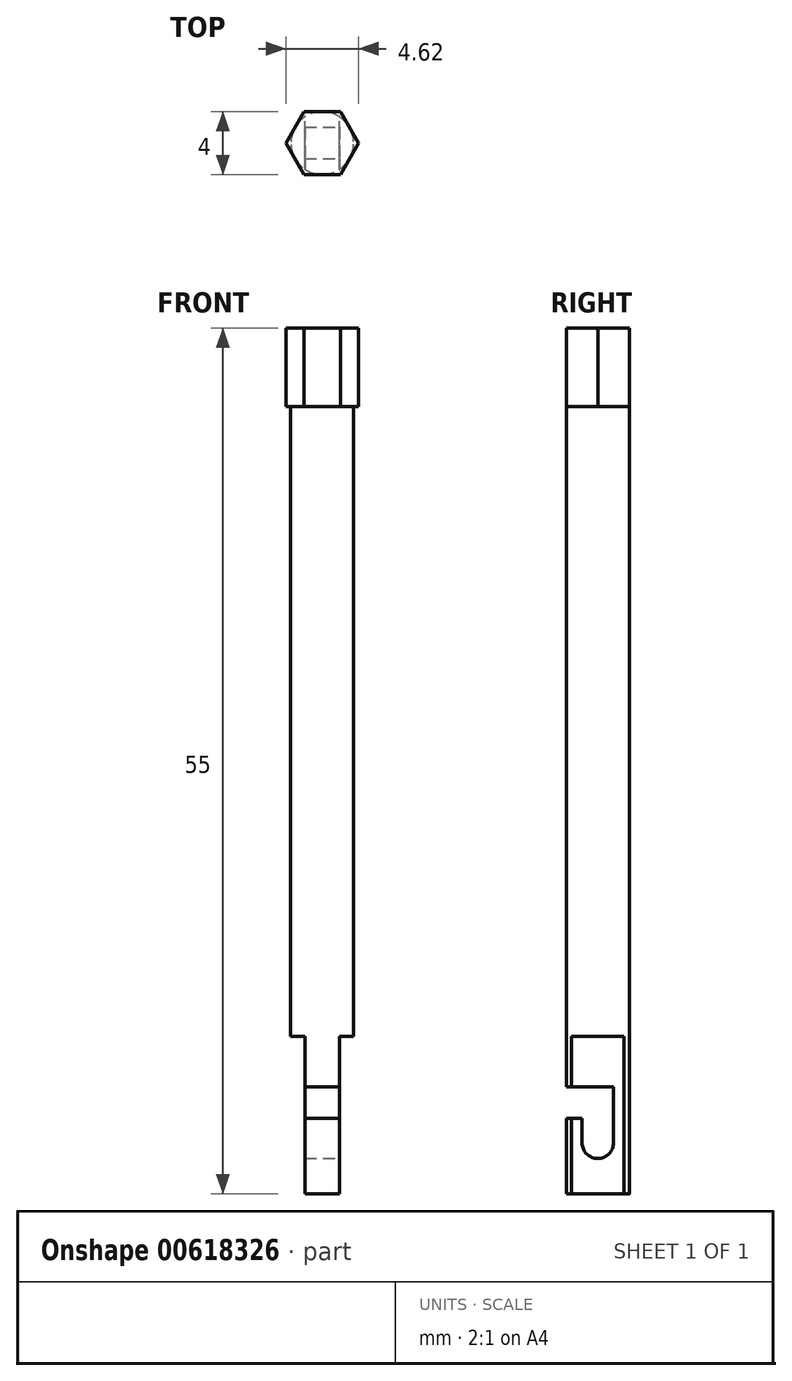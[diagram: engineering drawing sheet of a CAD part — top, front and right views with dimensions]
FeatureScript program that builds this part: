
annotation { "Feature Type Name" : "Feature", "Feature Type Description" : "" }
export const myFeature = defineFeature(function(context is Context, id is Id, definition is map)
    precondition{}
    {
        {
            var Q0;
            Q0=qCreatedBy(makeId("Top.planeOp"),FACE);
            var sketch = newSketch(context, id + "F0", { "sketchPlane" : qUnion([Q0])});
            skCircle(sketch, "E0", {"center": v(0, 0) * mm, "radius": 2 * mm});
            skSolve(sketch);
        }
        {
            var Q0;
            Q0 = qSketchRegion(id + "F0", true);
            extrude(context, id + "F1", {"entities" : qUnion([Q0]), "depth" : 40 * mm, "offsetDistance" : 25 * mm});
        }
        {
            var Q0;
            Q0=makeQuery(id+"F1.opExtrude","CAP_FACE",FACE,{"disambiguationData":[OSD([sQuery(id+"F0.wireOp",EDGE,"E0")])],"isStart":false});
            var sketch = newSketch(context, id + "F2", { "sketchPlane" : qUnion([Q0])});
            skCircle(sketch, "E1.cCircle", {"center": v(0, 0) * mm, "radius": 2 * mm, "construction": true});
            skLineSegment(sketch, "E1.0", {"start": v(-1.15, 2) * mm, "end": v(1.15, 2) * mm});
            skLineSegment(sketch, "E1.1", {"start": v(1.15, 2) * mm, "end": v(2.3, 0) * mm});
            skLineSegment(sketch, "E1.2", {"start": v(2.3, 0) * mm, "end": v(1.15, -2) * mm});
            skLineSegment(sketch, "E1.3", {"start": v(1.15, -2) * mm, "end": v(-1.15, -2) * mm});
            skLineSegment(sketch, "E1.4", {"start": v(-1.15, -2) * mm, "end": v(-2.3, 0) * mm});
            skLineSegment(sketch, "E1.5", {"start": v(-2.3, 0) * mm, "end": v(-1.15, 2) * mm});
            skPoint(sketch, "E1.0.midPoint", {"position": v(0, 2) * mm});
            skSolve(sketch);
        }
        {
            var Q0;
            {var subQ0=sQuery(id+"F2.wireOp",EDGE,"E1.5");var subQ1=sQuery(id+"F2.wireOp",EDGE,"E1.0");var subQ2=makeQuery(id+"F2.imprint","INTERSECT",VERTEX,{"derivedFrom":[subQ1,subQ0]});Q0=makeQuery(id+"F2.imprint","IMPRINT",FACE,{"disambiguationData":[TD([[makeQuery(id+"F2.imprint","IMPRINT",EDGE,{"disambiguationData":[TD([[subQ2,-1.0]])],"derivedFrom":subQ1}),-1.0]])]});}
            var Q1;
            {var subQ0=sQuery(id+"F2.wireOp",EDGE,"E1.5");var subQ1=sQuery(id+"F2.wireOp",EDGE,"E1.4");var subQ2=makeQuery(id+"F2.imprint","INTERSECT",VERTEX,{"derivedFrom":[subQ1,subQ0]});Q1=makeQuery(id+"F2.imprint","IMPRINT",FACE,{"disambiguationData":[TD([[makeQuery(id+"F2.imprint","IMPRINT",EDGE,{"disambiguationData":[TD([[subQ2,1.0]])],"derivedFrom":subQ1}),-1.0]])]});}
            var Q2;
            {var subQ0=sQuery(id+"F2.wireOp",EDGE,"E1.4");var subQ1=sQuery(id+"F2.wireOp",EDGE,"E1.3");var subQ2=makeQuery(id+"F2.imprint","INTERSECT",VERTEX,{"derivedFrom":[subQ1,subQ0]});Q2=makeQuery(id+"F2.imprint","IMPRINT",FACE,{"disambiguationData":[TD([[makeQuery(id+"F2.imprint","IMPRINT",EDGE,{"disambiguationData":[TD([[subQ2,1.0]])],"derivedFrom":subQ1}),-1.0]])]});}
            var Q3;
            {var subQ0=sQuery(id+"F2.wireOp",EDGE,"E1.3");var subQ1=sQuery(id+"F2.wireOp",EDGE,"E1.2");var subQ2=makeQuery(id+"F2.imprint","INTERSECT",VERTEX,{"derivedFrom":[subQ1,subQ0]});Q3=makeQuery(id+"F2.imprint","IMPRINT",FACE,{"disambiguationData":[TD([[makeQuery(id+"F2.imprint","IMPRINT",EDGE,{"disambiguationData":[TD([[subQ2,1.0]])],"derivedFrom":subQ1}),-1.0]])]});}
            var Q4;
            {var subQ0=sQuery(id+"F2.wireOp",EDGE,"E1.2");var subQ1=sQuery(id+"F2.wireOp",EDGE,"E1.1");var subQ2=makeQuery(id+"F2.imprint","INTERSECT",VERTEX,{"derivedFrom":[subQ1,subQ0]});Q4=makeQuery(id+"F2.imprint","IMPRINT",FACE,{"disambiguationData":[TD([[makeQuery(id+"F2.imprint","IMPRINT",EDGE,{"disambiguationData":[TD([[subQ2,1.0]])],"derivedFrom":subQ1}),-1.0]])]});}
            var Q5;
            {var subQ0=sQuery(id+"F2.wireOp",EDGE,"E1.1");var subQ1=sQuery(id+"F2.wireOp",EDGE,"E1.0");var subQ2=makeQuery(id+"F2.imprint","INTERSECT",VERTEX,{"derivedFrom":[subQ1,subQ0]});Q5=makeQuery(id+"F2.imprint","IMPRINT",FACE,{"disambiguationData":[TD([[makeQuery(id+"F2.imprint","IMPRINT",EDGE,{"disambiguationData":[TD([[subQ2,1.0]])],"derivedFrom":subQ1}),-1.0]])]});}
            var Q6;
            {var subQ0=makeQuery(id+"F1.opExtrude","CAP_EDGE",EDGE,{"disambiguationData":[OSD([sQuery(id+"F0.wireOp",EDGE,"E0")])],"isStart":false});var subQ4=makeQuery(id+"F2.imprint","INTERSECT",VERTEX,{"derivedFrom":[subQ0,sQuery(id+"F2.wireOp",EDGE,"E1.0")]});Q6=makeQuery(id+"F2.imprint","IMPRINT",FACE,{"disambiguationData":[TD([[makeQuery(id+"F2.imprint","IMPRINT",EDGE,{"disambiguationData":[TD([[subQ4,1.0]])],"derivedFrom":subQ0}),1.0]])]});}
            extrude(context, id + "F3", {"entities" : qUnion([Q0, Q1, Q2, Q3, Q4, Q5, Q6]), "operationType" : NewBodyOperationType.ADD, "depth" : 5 * mm, "offsetDistance" : 25 * mm});
        }
        {
            var Q0;
            Q0=makeQuery(id+"F1.opExtrude","CAP_FACE",FACE,{"disambiguationData":[OSD([sQuery(id+"F0.wireOp",EDGE,"E0")])],"isStart":true});
            var sketch = newSketch(context, id + "F4", { "sketchPlane" : qUnion([Q0])});
            skLineSegment(sketch, "E2.bottom", {"start": v(2.5, 2.5) * mm, "end": v(-2.5, 2.5) * mm});
            skLineSegment(sketch, "E2.top", {"start": v(2.5, -2.5) * mm, "end": v(-2.5, -2.5) * mm});
            skLineSegment(sketch, "E2.left", {"start": v(2.5, 2.5) * mm, "end": v(2.5, -2.5) * mm});
            skLineSegment(sketch, "E2.right", {"start": v(-2.5, 2.5) * mm, "end": v(-2.5, -2.5) * mm});
            skPoint(sketch, "E2.middle", {"position": v(0, 0) * mm});
            skLineSegment(sketch, "E3.bottom", {"start": v(1.1, 2) * mm, "end": v(-1.1, 2) * mm});
            skLineSegment(sketch, "E3.top", {"start": v(1.1, -2) * mm, "end": v(-1.1, -2) * mm});
            skLineSegment(sketch, "E3.left", {"start": v(1.1, 2) * mm, "end": v(1.1, -2) * mm});
            skLineSegment(sketch, "E3.right", {"start": v(-1.1, 2) * mm, "end": v(-1.1, -2) * mm});
            skSolve(sketch);
        }
        {
            var Q0;
            {var subQ0=makeQuery(id+"F1.opExtrude","CAP_EDGE",EDGE,{"disambiguationData":[OSD([sQuery(id+"F0.wireOp",EDGE,"E0")])],"isStart":true});var subQ5=sQuery(id+"F4.wireOp",EDGE,"E3.left");var subQ6=makeQuery(id+"F4.imprint","INTERSECT",VERTEX,{"disambiguationData":[OD(0.0)],"derivedFrom":[subQ0,subQ5]});Q0=makeQuery(id+"F4.imprint","IMPRINT",FACE,{"disambiguationData":[TD([[makeQuery(id+"F4.imprint","IMPRINT",EDGE,{"disambiguationData":[TD([[subQ6,-1.0]])],"derivedFrom":subQ5}),-1.0]])]});}
            extrude(context, id + "F5", {"entities" : qUnion([Q0]), "operationType" : NewBodyOperationType.ADD, "depth" : 10 * mm, "offsetDistance" : 25 * mm});
        }
        {
            var Q0;
            Q0=makeQuery(id+"F5.opExtrude","SWEPT_FACE",FACE,{"disambiguationData":[OSD([sQuery(id+"F4.wireOp",EDGE,"E3.left")])]});
            var sketch = newSketch(context, id + "F6", { "sketchPlane" : qUnion([Q0])});
            skPoint(sketch, "E4.firstSnap0", {"position": v(0, 0) * mm});
            skLineSegment(sketch, "E4.bottom", {"start": v(0, -3.2) * mm, "end": v(-2.6, -3.2) * mm});
            skLineSegment(sketch, "E4.top", {"start": v(0, -5.2) * mm, "end": v(-2.6, -5.2) * mm});
            skLineSegment(sketch, "E4.left", {"start": v(0, -3.2) * mm, "end": v(0, -5.2) * mm});
            skLineSegment(sketch, "E4.right", {"start": v(-2.6, -3.2) * mm, "end": v(-2.6, -5.2) * mm});
            skLineSegment(sketch, "E5.bottom", {"start": v(0, -7.75) * mm, "end": v(0, -7.75) * mm});
            skLineSegment(sketch, "E5.top", {"start": v(-1, 1.35) * mm, "end": v(1, 1.35) * mm});
            skLineSegment(sketch, "E5.left", {"start": v(-1, -6.75) * mm, "end": v(-1, 1.35) * mm});
            skLineSegment(sketch, "E5.right", {"start": v(1, -6.75) * mm, "end": v(1, 1.35) * mm});
            skPoint(sketch, "E5.middle", {"position": v(0, -3.2) * mm});
            skLineSegment(sketch, "E6", {"start": v(0, -3.2) * mm, "end": v(1, -3.2) * mm});
            skPoint(sketch, "E7.visualSharp", {"position": v(-1, -7.75) * mm});
            skArc(sketch, "E7.filletArc", {"start": v(-1, -6.75) * mm, "mid": v(-0.7, -7.45) * mm, "end": v(0, -7.75) * mm});
            skPoint(sketch, "E8.visualSharp", {"position": v(1, -7.75) * mm});
            skArc(sketch, "E8.filletArc", {"start": v(0, -7.75) * mm, "mid": v(0.7, -7.45) * mm, "end": v(1, -6.75) * mm});
            skSolve(sketch);
        }
        {
            var Q0;
            {var subQ0=sQuery(id+"F6.wireOp",EDGE,"E4.right");Q0=makeQuery(id+"F6.imprint","IMPRINT",FACE,{"disambiguationData":[TD([[makeQuery(id+"F6.imprint","IMPRINT",EDGE,{"derivedFrom":subQ0}),1.0]])]});}
            var Q1;
            {var subQ0=sQuery(id+"F6.wireOp",EDGE,"E5.left");var subQ1=sQuery(id+"F6.wireOp",EDGE,"E4.bottom");var subQ2=makeQuery(id+"F6.imprint","INTERSECT",VERTEX,{"derivedFrom":[subQ1,subQ0]});Q1=makeQuery(id+"F6.imprint","IMPRINT",FACE,{"disambiguationData":[TD([[makeQuery(id+"F6.imprint","IMPRINT",EDGE,{"disambiguationData":[TD([[subQ2,1.0]])],"derivedFrom":subQ0}),1.0]])]});}
            var Q2;
            {var subQ0=sQuery(id+"F6.wireOp",EDGE,"E4.left");Q2=makeQuery(id+"F6.imprint","IMPRINT",FACE,{"disambiguationData":[TD([[makeQuery(id+"F6.imprint","IMPRINT",EDGE,{"derivedFrom":subQ0}),-1.0]])]});}
            var Q3;
            {var subQ4=sQuery(id+"F6.wireOp",EDGE,"E4.left");Q3=makeQuery(id+"F6.imprint","IMPRINT",FACE,{"disambiguationData":[TD([[makeQuery(id+"F6.imprint","IMPRINT",EDGE,{"derivedFrom":subQ4}),1.0]])]});}
            extrude(context, id + "F7", {"entities" : qUnion([Q0, Q1, Q2, Q3]), "operationType" : NewBodyOperationType.REMOVE, "oppositeDirection" : true, "depth" : 25 * mm, "offsetDistance" : 25 * mm});
        }
    });
